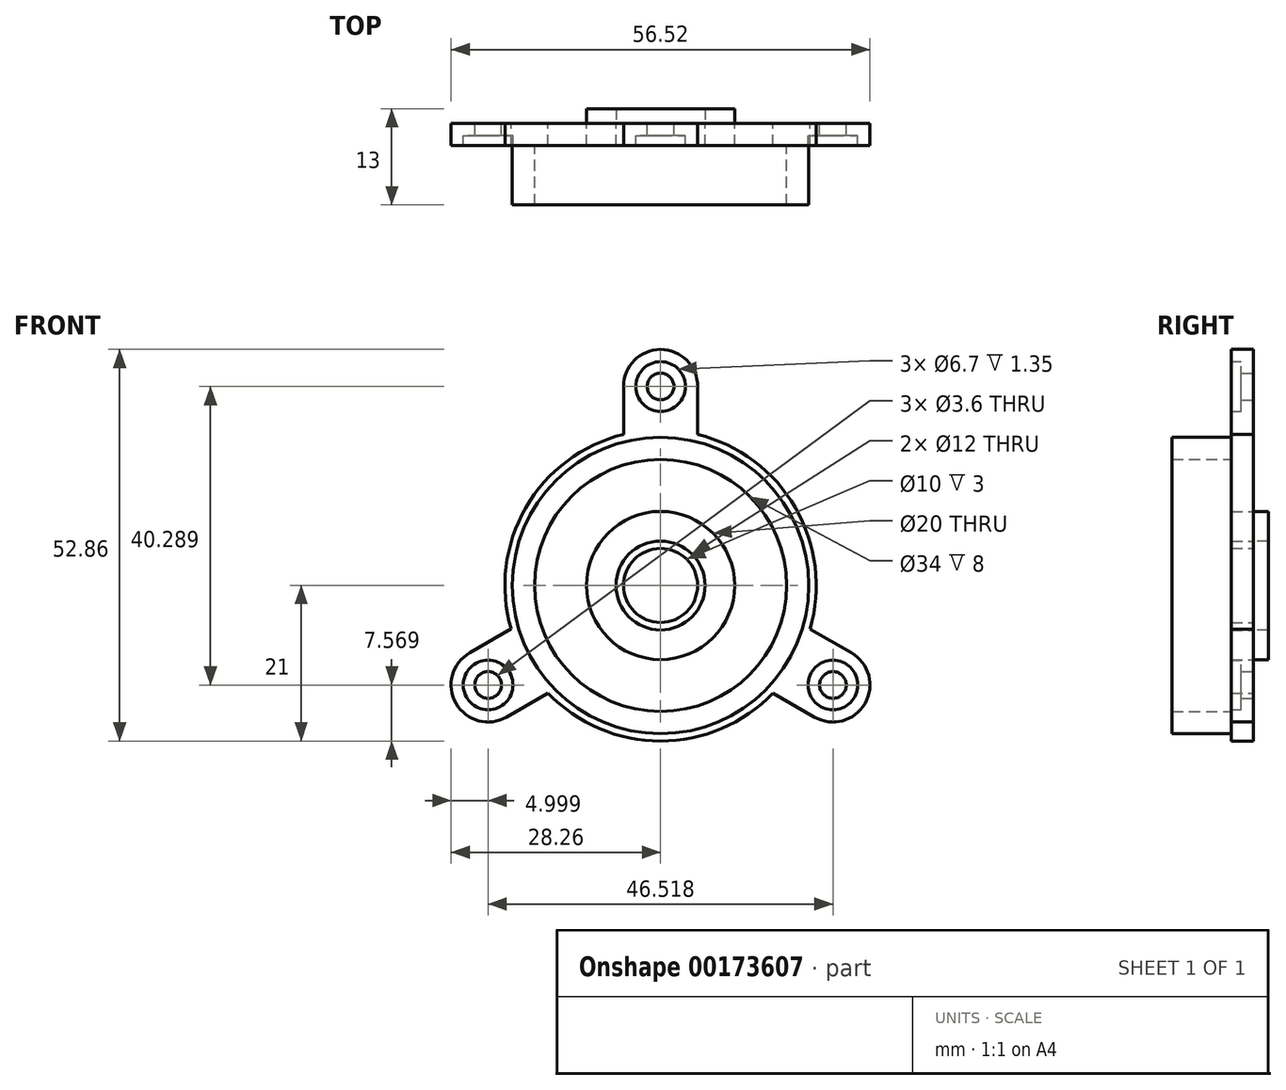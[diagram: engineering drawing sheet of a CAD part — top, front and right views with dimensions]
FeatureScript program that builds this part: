
annotation { "Feature Type Name" : "Feature", "Feature Type Description" : "" }
export const myFeature = defineFeature(function(context is Context, id is Id, definition is map)
    precondition{}
    {
        {
            var Q0;
            Q0=qCreatedBy(makeId("Front.planeOp"),FACE);
            var sketch = newSketch(context, id + "F0", { "sketchPlane" : qUnion([Q0])});
            skArc(sketch, "E0", {"start": v(-5, 20.4) * mm, "mid": v(-18.18, 10.5) * mm, "end": v(-20.16, -5.86) * mm});
            skLineSegment(sketch, "E1.left", {"start": v(5, 20.4) * mm, "end": v(5, 26.86) * mm});
            skLineSegment(sketch, "E1.right", {"start": v(-5, 20.4) * mm, "end": v(-5, 26.86) * mm});
            skArc(sketch, "E2", {"start": v(5, 26.86) * mm, "mid": v(0, 31.86) * mm, "end": v(-5, 26.86) * mm});
            skCircle(sketch, "E3", {"center": v(0, 26.86) * mm, "radius": 3.35 * mm});
            skCircle(sketch, "E4.1.0", {"center": v(-23.26, -13.43) * mm, "radius": 3.35 * mm});
            skLineSegment(sketch, "E4.1.1", {"start": v(-20.16, -5.86) * mm, "end": v(-25.76, -9.1) * mm});
            skArc(sketch, "E4.1.2", {"start": v(-25.76, -9.1) * mm, "mid": v(-27.6, -15.93) * mm, "end": v(-20.76, -17.76) * mm});
            skLineSegment(sketch, "E4.1.3", {"start": v(-15.17, -14.53) * mm, "end": v(-20.76, -17.76) * mm});
            skCircle(sketch, "E4.2.0", {"center": v(23.26, -13.43) * mm, "radius": 3.35 * mm});
            skLineSegment(sketch, "E4.2.1", {"start": v(15.16, -14.53) * mm, "end": v(20.76, -17.76) * mm});
            skArc(sketch, "E4.2.2", {"start": v(20.76, -17.76) * mm, "mid": v(27.59, -15.93) * mm, "end": v(25.76, -9.1) * mm});
            skLineSegment(sketch, "E4.2.3", {"start": v(20.16, -5.87) * mm, "end": v(25.76, -9.1) * mm});
            skArc(sketch, "E5.trimOffspring", {"start": v(-15.17, -14.53) * mm, "mid": v(0, -21) * mm, "end": v(15.16, -14.53) * mm});
            skArc(sketch, "E6.trimOffspring", {"start": v(20.16, -5.87) * mm, "mid": v(18.19, 10.5) * mm, "end": v(5, 20.4) * mm});
            skCircle(sketch, "E7", {"center": v(0, 0) * mm, "radius": 20 * mm});
            skCircle(sketch, "E8", {"center": v(0, 0) * mm, "radius": 5 * mm});
            skCircle(sketch, "E9", {"center": v(0, 0) * mm, "radius": 17 * mm});
            skCircle(sketch, "E10", {"center": v(0, 0) * mm, "radius": 6 * mm});
            skCircle(sketch, "E11", {"center": v(0, 26.86) * mm, "radius": 1.8 * mm});
            skCircle(sketch, "E12", {"center": v(-23.26, -13.43) * mm, "radius": 1.8 * mm});
            skCircle(sketch, "E13", {"center": v(23.26, -13.43) * mm, "radius": 1.8 * mm});
            skCircle(sketch, "E14", {"center": v(0, 0) * mm, "radius": 10 * mm});
            skSolve(sketch);
        }
        {
            var Q0;
            Q0=makeQuery(id+"F0.imprint","IMPRINT",FACE,{"disambiguationData":[TD([[makeQuery(id+"F0.imprint","IMPRINT",EDGE,{"derivedFrom":sQuery(id+"F0.wireOp",EDGE,"E0")}),1.0]])]});
            var Q1;
            Q1=makeQuery(id+"F0.imprint","IMPRINT",FACE,{"disambiguationData":[TD([[makeQuery(id+"F0.imprint","IMPRINT",EDGE,{"derivedFrom":sQuery(id+"F0.wireOp",EDGE,"E9")}),1.0]])]});
            var Q2;
            Q2=makeQuery(id+"F0.imprint","IMPRINT",FACE,{"disambiguationData":[TD([[makeQuery(id+"F0.imprint","IMPRINT",EDGE,{"derivedFrom":sQuery(id+"F0.wireOp",EDGE,"E7")}),1.0]])]});
            var Q3;
            Q3=makeQuery(id+"F0.imprint","IMPRINT",FACE,{"disambiguationData":[TD([[makeQuery(id+"F0.imprint","IMPRINT",EDGE,{"derivedFrom":sQuery(id+"F0.wireOp",EDGE,"E8")}),-1.0]])]});
            extrude(context, id + "F1", {"entities" : qUnion([Q0, Q1, Q2, Q3]), "depth" : 3 * mm});
        }
        {
            var Q0;
            Q0=makeQuery(id+"F0.imprint","IMPRINT",FACE,{"disambiguationData":[TD([[makeQuery(id+"F0.imprint","IMPRINT",EDGE,{"derivedFrom":sQuery(id+"F0.wireOp",EDGE,"E7")}),1.0]])]});
            extrude(context, id + "F2", {"entities" : qUnion([Q0]), "operationType" : NewBodyOperationType.ADD, "depth" : 11 * mm});
        }
        {
            var Q0;
            Q0=makeQuery(id+"F0.imprint","IMPRINT",FACE,{"disambiguationData":[TD([[makeQuery(id+"F0.imprint","IMPRINT",EDGE,{"derivedFrom":sQuery(id+"F0.wireOp",EDGE,"E3")}),1.0]])]});
            var Q1;
            Q1=makeQuery(id+"F0.imprint","IMPRINT",FACE,{"disambiguationData":[TD([[makeQuery(id+"F0.imprint","IMPRINT",EDGE,{"derivedFrom":sQuery(id+"F0.wireOp",EDGE,"E4.2.0")}),1.0]])]});
            var Q2;
            Q2=makeQuery(id+"F0.imprint","IMPRINT",FACE,{"disambiguationData":[TD([[makeQuery(id+"F0.imprint","IMPRINT",EDGE,{"derivedFrom":sQuery(id+"F0.wireOp",EDGE,"E4.1.0")}),1.0]])]});
            extrude(context, id + "F3", {"entities" : qUnion([Q0, Q1, Q2]), "operationType" : NewBodyOperationType.ADD, "depth" : 1.65 * mm});
        }
        {
            var Q0;
            Q0=makeQuery(id+"F0.imprint","IMPRINT",FACE,{"disambiguationData":[TD([[makeQuery(id+"F0.imprint","IMPRINT",EDGE,{"derivedFrom":sQuery(id+"F0.wireOp",EDGE,"E10")}),-1.0]])]});
            extrude(context, id + "F4", {"entities" : qUnion([Q0]), "oppositeDirection" : true, "depth" : 2 * mm});
        }
        {
            var Q0;
            Q0=makeQuery(id+"F4.opExtrude","CAP_FACE",FACE,{"disambiguationData":[OSD([sQuery(id+"F0.wireOp",EDGE,"E10"),sQuery(id+"F0.wireOp",EDGE,"E14")])],"isStart":true});
            extrude(context, id + "F5", {"entities" : qUnion([Q0]), "depth" : 3 * mm});
        }
    });
